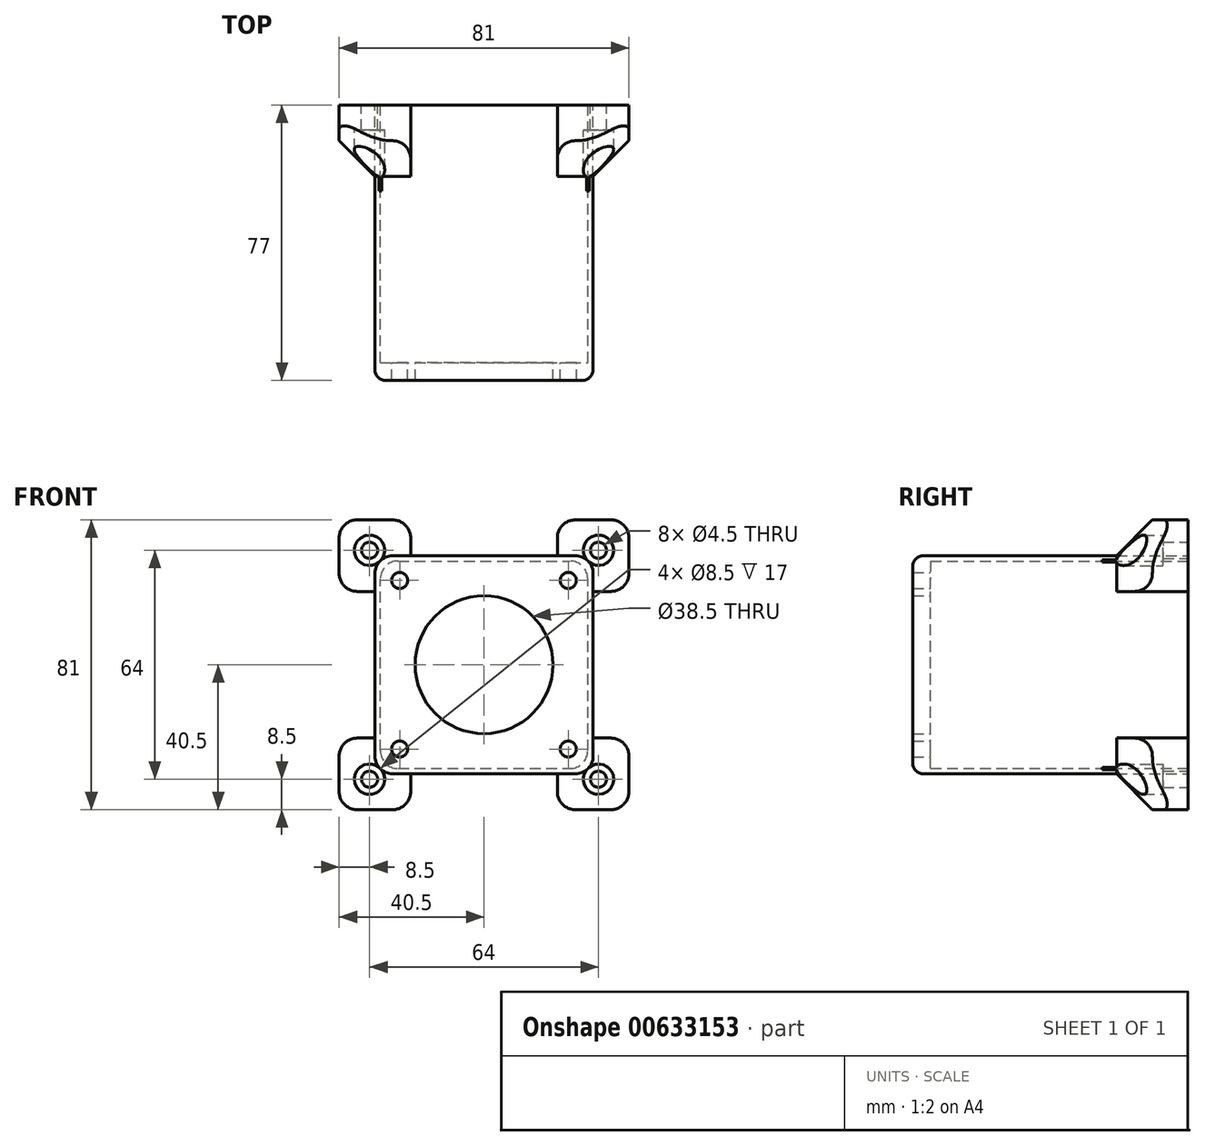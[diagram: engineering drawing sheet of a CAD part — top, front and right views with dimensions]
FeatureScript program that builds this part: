
annotation { "Feature Type Name" : "Feature", "Feature Type Description" : "" }
export const myFeature = defineFeature(function(context is Context, id is Id, definition is map)
    precondition{}
    {
        {
            var Q0;
            Q0=qCreatedBy(makeId("Front.planeOp"),FACE);
            var sketch = newSketch(context, id + "F0", { "sketchPlane" : qUnion([Q0])});
            skLineSegment(sketch, "E0.bottom", {"start": v(-29, -29) * mm, "end": v(29, -29) * mm});
            skLineSegment(sketch, "E0.top", {"start": v(-29, 29) * mm, "end": v(29, 29) * mm});
            skLineSegment(sketch, "E0.left", {"start": v(-29, -29) * mm, "end": v(-29, 29) * mm});
            skLineSegment(sketch, "E0.right", {"start": v(29, -29) * mm, "end": v(29, 29) * mm});
            skPoint(sketch, "E0.middle", {"position": v(0, 0) * mm});
            skLineSegment(sketch, "E1.bottom", {"start": v(-30.5, -30.5) * mm, "end": v(30.5, -30.5) * mm});
            skLineSegment(sketch, "E1.top", {"start": v(-30.5, 30.5) * mm, "end": v(30.5, 30.5) * mm});
            skLineSegment(sketch, "E1.left", {"start": v(-30.5, -30.5) * mm, "end": v(-30.5, 30.5) * mm});
            skLineSegment(sketch, "E1.right", {"start": v(30.5, -30.5) * mm, "end": v(30.5, 30.5) * mm});
            skLineSegment(sketch, "E2", {"start": v(-30.5, 20.5) * mm, "end": v(-40.5, 20.5) * mm});
            skLineSegment(sketch, "E3", {"start": v(-40.5, 20.5) * mm, "end": v(-40.5, 40.5) * mm});
            skLineSegment(sketch, "E4", {"start": v(-40.5, 40.5) * mm, "end": v(-20.5, 40.5) * mm});
            skLineSegment(sketch, "E5", {"start": v(-20.5, 40.5) * mm, "end": v(-20.5, 30.5) * mm});
            skLineSegment(sketch, "E6", {"start": v(20.5, 30.5) * mm, "end": v(20.5, 40.5) * mm});
            skLineSegment(sketch, "E7", {"start": v(20.5, 40.5) * mm, "end": v(40.5, 40.5) * mm});
            skLineSegment(sketch, "E8", {"start": v(40.5, 40.5) * mm, "end": v(40.5, 20.5) * mm});
            skLineSegment(sketch, "E9", {"start": v(40.5, 20.5) * mm, "end": v(30.5, 20.5) * mm});
            skLineSegment(sketch, "E10", {"start": v(30.5, -20.5) * mm, "end": v(40.5, -20.5) * mm});
            skLineSegment(sketch, "E11", {"start": v(40.5, -20.5) * mm, "end": v(40.5, -40.5) * mm});
            skLineSegment(sketch, "E12", {"start": v(40.5, -40.5) * mm, "end": v(20.5, -40.5) * mm});
            skLineSegment(sketch, "E13", {"start": v(20.5, -40.5) * mm, "end": v(20.5, -30.5) * mm});
            skLineSegment(sketch, "E14", {"start": v(-20.5, -30.5) * mm, "end": v(-20.5, -40.5) * mm});
            skLineSegment(sketch, "E15", {"start": v(-20.5, -40.5) * mm, "end": v(-40.5, -40.5) * mm});
            skLineSegment(sketch, "E16", {"start": v(-40.5, -40.5) * mm, "end": v(-40.5, -20.5) * mm});
            skLineSegment(sketch, "E17", {"start": v(-40.5, -20.5) * mm, "end": v(-30.5, -20.5) * mm});
            skCircle(sketch, "E18", {"center": v(0, 0) * mm, "radius": 19.25 * mm});
            skSolve(sketch);
        }
        {
            var Q0;
            Q0=qCreatedBy(makeId("Front.planeOp"),FACE);
            var sketch = newSketch(context, id + "F1", { "sketchPlane" : qUnion([Q0])});
            skPoint(sketch, "E19", {"position": v(-32, -32) * mm});
            skPoint(sketch, "E20", {"position": v(-32, 32) * mm});
            skPoint(sketch, "E21", {"position": v(32, 32) * mm});
            skPoint(sketch, "E22", {"position": v(32, -32) * mm});
            skSolve(sketch);
        }
        {
            var Q0;
            Q0=qCreatedBy(makeId("Front.planeOp"),FACE);
            var sketch = newSketch(context, id + "F2", { "sketchPlane" : qUnion([Q0])});
            skPoint(sketch, "E23", {"position": v(23.57, 23.57) * mm});
            skPoint(sketch, "E24", {"position": v(-23.57, 23.57) * mm});
            skPoint(sketch, "E25", {"position": v(-23.57, -23.57) * mm});
            skPoint(sketch, "E26", {"position": v(23.57, -23.57) * mm});
            skSolve(sketch);
        }
        {
            var Q0;
            Q0=makeQuery(id+"F0.imprint","IMPRINT",FACE,{"disambiguationData":[TD([[makeQuery(id+"F0.imprint","IMPRINT",EDGE,{"derivedFrom":sQuery(id+"F0.wireOp",EDGE,"E0.bottom")}),-1.0]])]});
            extrude(context, id + "F3", {"entities" : qUnion([Q0]), "depth" : 77 * mm, "offsetDistance" : 25 * mm});
        }
        {
            var Q0;
            {var subQ0=sQuery(id+"F0.wireOp",EDGE,"E2");Q0=makeQuery(id+"F0.imprint","IMPRINT",FACE,{"disambiguationData":[TD([[makeQuery(id+"F0.imprint","IMPRINT",EDGE,{"derivedFrom":subQ0}),-1.0]])]});}
            var Q1;
            {var subQ0=sQuery(id+"F0.wireOp",EDGE,"E6");Q1=makeQuery(id+"F0.imprint","IMPRINT",FACE,{"disambiguationData":[TD([[makeQuery(id+"F0.imprint","IMPRINT",EDGE,{"derivedFrom":subQ0}),-1.0]])]});}
            var Q2;
            {var subQ0=sQuery(id+"F0.wireOp",EDGE,"E10");Q2=makeQuery(id+"F0.imprint","IMPRINT",FACE,{"disambiguationData":[TD([[makeQuery(id+"F0.imprint","IMPRINT",EDGE,{"derivedFrom":subQ0}),-1.0]])]});}
            var Q3;
            {var subQ0=sQuery(id+"F0.wireOp",EDGE,"E14");Q3=makeQuery(id+"F0.imprint","IMPRINT",FACE,{"disambiguationData":[TD([[makeQuery(id+"F0.imprint","IMPRINT",EDGE,{"derivedFrom":subQ0}),-1.0]])]});}
            extrude(context, id + "F4", {"entities" : qUnion([Q0, Q1, Q2, Q3]), "operationType" : NewBodyOperationType.ADD, "depth" : 5 * mm, "offsetDistance" : 25 * mm});
        }
        {
            var Q0;
            Q0=makeQuery(id+"F0.imprint","IMPRINT",FACE,{"disambiguationData":[TD([[makeQuery(id+"F0.imprint","IMPRINT",EDGE,{"derivedFrom":sQuery(id+"F0.wireOp",EDGE,"E0.bottom")}),-1.0]])]});
            var Q1;
            Q1=makeQuery(id+"F0.imprint","IMPRINT",FACE,{"disambiguationData":[TD([[makeQuery(id+"F0.imprint","IMPRINT",EDGE,{"derivedFrom":sQuery(id+"F0.wireOp",EDGE,"E0.bottom")}),1.0]])]});
            extrude(context, id + "F5", {"entities" : qUnion([Q0, Q1]), "operationType" : NewBodyOperationType.ADD, "depth" : 77 * mm, "offsetDistance" : 25 * mm, "hasSecondDirection" : true, "secondDirectionOppositeDirection" : false, "secondDirectionDepth" : 72 * mm});
        }
        {
            var Q0;
            Q0=makeQuery(id+"F0.imprint","IMPRINT",FACE,{"disambiguationData":[TD([[makeQuery(id+"F0.imprint","IMPRINT",EDGE,{"derivedFrom":sQuery(id+"F0.wireOp",EDGE,"E18")}),1.0]])]});
            extrude(context, id + "F6", {"entities" : qUnion([Q0]), "operationType" : NewBodyOperationType.REMOVE, "depth" : 91.6 * mm, "offsetDistance" : 25 * mm});
        }
        {
            var Q0;
            Q0=makeQuery(id+"F3.opExtrude","SWEPT_EDGE",EDGE,{"disambiguationData":[OSD([sQuery(id+"F0.wireOp",EDGE,"E1.top"),sQuery(id+"F0.wireOp",EDGE,"E1.left")])]});
            var Q1;
            Q1=makeQuery(id+"F3.opExtrude","SWEPT_EDGE",EDGE,{"disambiguationData":[OSD([sQuery(id+"F0.wireOp",EDGE,"E1.bottom"),sQuery(id+"F0.wireOp",EDGE,"E1.left")])]});
            var Q2;
            Q2=makeQuery(id+"F3.opExtrude","SWEPT_EDGE",EDGE,{"disambiguationData":[OSD([sQuery(id+"F0.wireOp",EDGE,"E1.bottom"),sQuery(id+"F0.wireOp",EDGE,"E1.right")])]});
            var Q3;
            Q3=makeQuery(id+"F3.opExtrude","SWEPT_EDGE",EDGE,{"disambiguationData":[OSD([sQuery(id+"F0.wireOp",EDGE,"E1.top"),sQuery(id+"F0.wireOp",EDGE,"E1.right")])]});
            var Q4;
            Q4=makeQuery(id+"F3.opExtrude","SWEPT_EDGE",EDGE,{"disambiguationData":[OSD([sQuery(id+"F0.wireOp",EDGE,"E0.bottom"),sQuery(id+"F0.wireOp",EDGE,"E0.left")])]});
            var Q5;
            Q5=makeQuery(id+"F3.opExtrude","SWEPT_EDGE",EDGE,{"disambiguationData":[OSD([sQuery(id+"F0.wireOp",EDGE,"E0.top"),sQuery(id+"F0.wireOp",EDGE,"E0.left")])]});
            var Q6;
            Q6=makeQuery(id+"F3.opExtrude","SWEPT_EDGE",EDGE,{"disambiguationData":[OSD([sQuery(id+"F0.wireOp",EDGE,"E0.top"),sQuery(id+"F0.wireOp",EDGE,"E0.right")])]});
            var Q7;
            Q7=makeQuery(id+"F3.opExtrude","SWEPT_EDGE",EDGE,{"disambiguationData":[OSD([sQuery(id+"F0.wireOp",EDGE,"E0.bottom"),sQuery(id+"F0.wireOp",EDGE,"E0.right")])]});
            fillet(context, id + "F7", {"entities" : qUnion([Q0, Q1, Q2, Q3, Q4, Q5, Q6, Q7]), "radius" : 5 * mm, "tangentPropagation" : true, "allowEdgeOverflow" : false});
        }
        {
            var Q0;
            Q0=sQuery(id+"F2.wireOp",VERTEX,"E23");
            var Q1;
            Q1=sQuery(id+"F2.wireOp",VERTEX,"E25");
            var Q2;
            Q2=sQuery(id+"F2.wireOp",VERTEX,"E24");
            var Q3;
            Q3=sQuery(id+"F2.wireOp",VERTEX,"E26");
            var Q4;
            Q4=makeQuery(id+"F3.opExtrude","SWEPT_BODY",BODY,{"disambiguationData":[OSD([sQuery(id+"F0.wireOp",EDGE,"E0.bottom"),sQuery(id+"F0.wireOp",EDGE,"E0.top"),sQuery(id+"F0.wireOp",EDGE,"E0.left"),sQuery(id+"F0.wireOp",EDGE,"E0.right"),sQuery(id+"F0.wireOp",EDGE,"E1.bottom"),sQuery(id+"F0.wireOp",EDGE,"E1.top"),sQuery(id+"F0.wireOp",EDGE,"E1.left"),sQuery(id+"F0.wireOp",EDGE,"E1.right")])]});
            hole(context, id + "F8", {"style" : HoleStyle.SIMPLE, "endStyle" : HoleEndStyle.THROUGH, "oppositeDirection" : true, "holeDiameter" : 4.5 * mm, "majorDiameter" : 5 * mm, "isTappedThrough" : true, "tappedDepth" : 12 * mm, "tapClearance" : 3, "startFromSketch" : true, "locations" : qUnion([Q0, Q1, Q2, Q3]), "scope" : qUnion([Q4])});
        }
        {
            var Q0;
            Q0=makeQuery(id+"F3.opExtrude","CAP_EDGE",EDGE,{"disambiguationData":[OSD([sQuery(id+"F0.wireOp",EDGE,"E1.left")])],"isStart":false});
            fillet(context, id + "F9", {"entities" : qUnion([Q0]), "radius" : 3 * mm, "tangentPropagation" : true, "allowEdgeOverflow" : false});
        }
        {
            var Q0;
            {var subQ0=sQuery(id+"F0.wireOp",EDGE,"E1.right");var subQ1=sQuery(id+"F0.wireOp",EDGE,"E1.bottom");Q0=makeQuery(id+"F7.opFillet","BLEND_EDGE",EDGE,{"blendedFrom":[makeQuery(id+"F3.opExtrude","SWEPT_EDGE",EDGE,{"disambiguationData":[OSD([subQ1,subQ0])]}),makeQuery(id+"F4.opExtrude","CAP_FACE",FACE,{"disambiguationData":[OSD([subQ1,subQ0,sQuery(id+"F0.wireOp",EDGE,"E10"),sQuery(id+"F0.wireOp",EDGE,"E11"),sQuery(id+"F0.wireOp",EDGE,"E12"),sQuery(id+"F0.wireOp",EDGE,"E13")])],"isStart":false})],"blendedInto":[makeQuery(id+"F4.opExtrude","CAP_FACE",FACE,{"disambiguationData":[OSD([subQ1,subQ0,sQuery(id+"F0.wireOp",EDGE,"E10"),sQuery(id+"F0.wireOp",EDGE,"E11"),sQuery(id+"F0.wireOp",EDGE,"E12"),sQuery(id+"F0.wireOp",EDGE,"E13")])],"isStart":false})]});}
            var Q1;
            {var subQ0=sQuery(id+"F0.wireOp",EDGE,"E1.right");var subQ1=sQuery(id+"F0.wireOp",EDGE,"E1.top");Q1=makeQuery(id+"F7.opFillet","BLEND_EDGE",EDGE,{"blendedFrom":[makeQuery(id+"F3.opExtrude","SWEPT_EDGE",EDGE,{"disambiguationData":[OSD([subQ1,subQ0])]}),makeQuery(id+"F4.opExtrude","CAP_FACE",FACE,{"disambiguationData":[OSD([subQ1,subQ0,sQuery(id+"F0.wireOp",EDGE,"E6"),sQuery(id+"F0.wireOp",EDGE,"E7"),sQuery(id+"F0.wireOp",EDGE,"E8"),sQuery(id+"F0.wireOp",EDGE,"E9")])],"isStart":false})],"blendedInto":[makeQuery(id+"F4.opExtrude","CAP_FACE",FACE,{"disambiguationData":[OSD([subQ1,subQ0,sQuery(id+"F0.wireOp",EDGE,"E6"),sQuery(id+"F0.wireOp",EDGE,"E7"),sQuery(id+"F0.wireOp",EDGE,"E8"),sQuery(id+"F0.wireOp",EDGE,"E9")])],"isStart":false})]});}
            var Q2;
            {var subQ0=sQuery(id+"F0.wireOp",EDGE,"E1.left");var subQ1=sQuery(id+"F0.wireOp",EDGE,"E1.top");Q2=makeQuery(id+"F7.opFillet","BLEND_EDGE",EDGE,{"blendedFrom":[makeQuery(id+"F3.opExtrude","SWEPT_EDGE",EDGE,{"disambiguationData":[OSD([subQ1,subQ0])]}),makeQuery(id+"F4.opExtrude","CAP_FACE",FACE,{"disambiguationData":[OSD([subQ1,subQ0,sQuery(id+"F0.wireOp",EDGE,"E2"),sQuery(id+"F0.wireOp",EDGE,"E3"),sQuery(id+"F0.wireOp",EDGE,"E4"),sQuery(id+"F0.wireOp",EDGE,"E5")])],"isStart":false})],"blendedInto":[makeQuery(id+"F4.opExtrude","CAP_FACE",FACE,{"disambiguationData":[OSD([subQ1,subQ0,sQuery(id+"F0.wireOp",EDGE,"E2"),sQuery(id+"F0.wireOp",EDGE,"E3"),sQuery(id+"F0.wireOp",EDGE,"E4"),sQuery(id+"F0.wireOp",EDGE,"E5")])],"isStart":false})]});}
            var Q3;
            {var subQ0=sQuery(id+"F0.wireOp",EDGE,"E1.left");var subQ1=sQuery(id+"F0.wireOp",EDGE,"E1.bottom");Q3=makeQuery(id+"F7.opFillet","BLEND_EDGE",EDGE,{"blendedFrom":[makeQuery(id+"F3.opExtrude","SWEPT_EDGE",EDGE,{"disambiguationData":[OSD([subQ1,subQ0])]}),makeQuery(id+"F4.opExtrude","CAP_FACE",FACE,{"disambiguationData":[OSD([subQ1,subQ0,sQuery(id+"F0.wireOp",EDGE,"E14"),sQuery(id+"F0.wireOp",EDGE,"E15"),sQuery(id+"F0.wireOp",EDGE,"E16"),sQuery(id+"F0.wireOp",EDGE,"E17")])],"isStart":false})],"blendedInto":[makeQuery(id+"F4.opExtrude","CAP_FACE",FACE,{"disambiguationData":[OSD([subQ1,subQ0,sQuery(id+"F0.wireOp",EDGE,"E14"),sQuery(id+"F0.wireOp",EDGE,"E15"),sQuery(id+"F0.wireOp",EDGE,"E16"),sQuery(id+"F0.wireOp",EDGE,"E17")])],"isStart":false})]});}
            chamfer(context, id + "F10", {"entities" : qUnion([Q0, Q1, Q2, Q3]), "width" : 15 * mm, "tangentPropagation" : true});
        }
        {
            var Q0;
            Q0=sQuery(id+"F1.wireOp",VERTEX,"E19");
            var Q1;
            Q1=sQuery(id+"F1.wireOp",VERTEX,"E22");
            var Q2;
            Q2=sQuery(id+"F1.wireOp",VERTEX,"E21");
            var Q3;
            Q3=sQuery(id+"F1.wireOp",VERTEX,"E20");
            var Q4;
            Q4=makeQuery(id+"F3.opExtrude","SWEPT_BODY",BODY,{"disambiguationData":[OSD([sQuery(id+"F0.wireOp",EDGE,"E0.bottom"),sQuery(id+"F0.wireOp",EDGE,"E0.top"),sQuery(id+"F0.wireOp",EDGE,"E0.left"),sQuery(id+"F0.wireOp",EDGE,"E0.right"),sQuery(id+"F0.wireOp",EDGE,"E1.bottom"),sQuery(id+"F0.wireOp",EDGE,"E1.top"),sQuery(id+"F0.wireOp",EDGE,"E1.left"),sQuery(id+"F0.wireOp",EDGE,"E1.right")])]});
            hole(context, id + "F11", {"style" : HoleStyle.SIMPLE, "endStyle" : HoleEndStyle.THROUGH, "oppositeDirection" : true, "holeDiameter" : 4.5 * mm, "majorDiameter" : 5 * mm, "isTappedThrough" : true, "tappedDepth" : 12 * mm, "tapClearance" : 3, "startFromSketch" : true, "locations" : qUnion([Q0, Q1, Q2, Q3]), "scope" : qUnion([Q4])});
        }
        {
            var Q0;
            Q0=qCreatedBy(makeId("Front.planeOp"),FACE);
            var sketch = newSketch(context, id + "F12", { "sketchPlane" : qUnion([Q0])});
            skCircle(sketch, "E27", {"center": v(-32, 32) * mm, "radius": 4.25 * mm});
            skCircle(sketch, "E28", {"center": v(32, -32) * mm, "radius": 4.25 * mm});
            skCircle(sketch, "E29", {"center": v(32, 32) * mm, "radius": 4.25 * mm});
            skCircle(sketch, "E30", {"center": v(-32, -32) * mm, "radius": 4.25 * mm});
            skSolve(sketch);
        }
        {
            var Q0;
            Q0 = qSketchRegion(id + "F12", true);
            extrude(context, id + "F13", {"entities" : qUnion([Q0]), "operationType" : NewBodyOperationType.REMOVE, "depth" : 24 * mm, "offsetDistance" : 25 * mm, "hasSecondDirection" : true, "secondDirectionOppositeDirection" : false, "secondDirectionDepth" : 7 * mm});
        }
        {
            var Q0;
            Q0=makeQuery(id+"F4.opExtrude","SWEPT_EDGE",EDGE,{"disambiguationData":[OSD([sQuery(id+"F0.wireOp",EDGE,"E7"),sQuery(id+"F0.wireOp",EDGE,"E8")])]});
            var Q1;
            Q1=makeQuery(id+"F4.opExtrude","SWEPT_EDGE",EDGE,{"disambiguationData":[OSD([sQuery(id+"F0.wireOp",EDGE,"E6"),sQuery(id+"F0.wireOp",EDGE,"E7")])]});
            var Q2;
            Q2=makeQuery(id+"F4.opExtrude","SWEPT_EDGE",EDGE,{"disambiguationData":[OSD([sQuery(id+"F0.wireOp",EDGE,"E8"),sQuery(id+"F0.wireOp",EDGE,"E9")])]});
            var Q3;
            Q3=makeQuery(id+"F4.opExtrude","SWEPT_EDGE",EDGE,{"disambiguationData":[OSD([sQuery(id+"F0.wireOp",EDGE,"E10"),sQuery(id+"F0.wireOp",EDGE,"E11")])]});
            var Q4;
            Q4=makeQuery(id+"F4.opExtrude","SWEPT_EDGE",EDGE,{"disambiguationData":[OSD([sQuery(id+"F0.wireOp",EDGE,"E11"),sQuery(id+"F0.wireOp",EDGE,"E12")])]});
            var Q5;
            Q5=makeQuery(id+"F4.opExtrude","SWEPT_EDGE",EDGE,{"disambiguationData":[OSD([sQuery(id+"F0.wireOp",EDGE,"E12"),sQuery(id+"F0.wireOp",EDGE,"E13")])]});
            var Q6;
            Q6=makeQuery(id+"F4.opExtrude","SWEPT_EDGE",EDGE,{"disambiguationData":[OSD([sQuery(id+"F0.wireOp",EDGE,"E14"),sQuery(id+"F0.wireOp",EDGE,"E15")])]});
            var Q7;
            Q7=makeQuery(id+"F4.opExtrude","SWEPT_EDGE",EDGE,{"disambiguationData":[OSD([sQuery(id+"F0.wireOp",EDGE,"E15"),sQuery(id+"F0.wireOp",EDGE,"E16")])]});
            var Q8;
            Q8=makeQuery(id+"F4.opExtrude","SWEPT_EDGE",EDGE,{"disambiguationData":[OSD([sQuery(id+"F0.wireOp",EDGE,"E16"),sQuery(id+"F0.wireOp",EDGE,"E17")])]});
            var Q9;
            Q9=makeQuery(id+"F4.opExtrude","SWEPT_EDGE",EDGE,{"disambiguationData":[OSD([sQuery(id+"F0.wireOp",EDGE,"E2"),sQuery(id+"F0.wireOp",EDGE,"E3")])]});
            var Q10;
            Q10=makeQuery(id+"F4.opExtrude","SWEPT_EDGE",EDGE,{"disambiguationData":[OSD([sQuery(id+"F0.wireOp",EDGE,"E3"),sQuery(id+"F0.wireOp",EDGE,"E4")])]});
            var Q11;
            Q11=makeQuery(id+"F4.opExtrude","SWEPT_EDGE",EDGE,{"disambiguationData":[OSD([sQuery(id+"F0.wireOp",EDGE,"E4"),sQuery(id+"F0.wireOp",EDGE,"E5")])]});
            fillet(context, id + "F14", {"entities" : qUnion([Q0, Q1, Q2, Q3, Q4, Q5, Q6, Q7, Q8, Q9, Q10, Q11]), "radius" : 5 * mm, "tangentPropagation" : true, "allowEdgeOverflow" : false});
        }
    });
